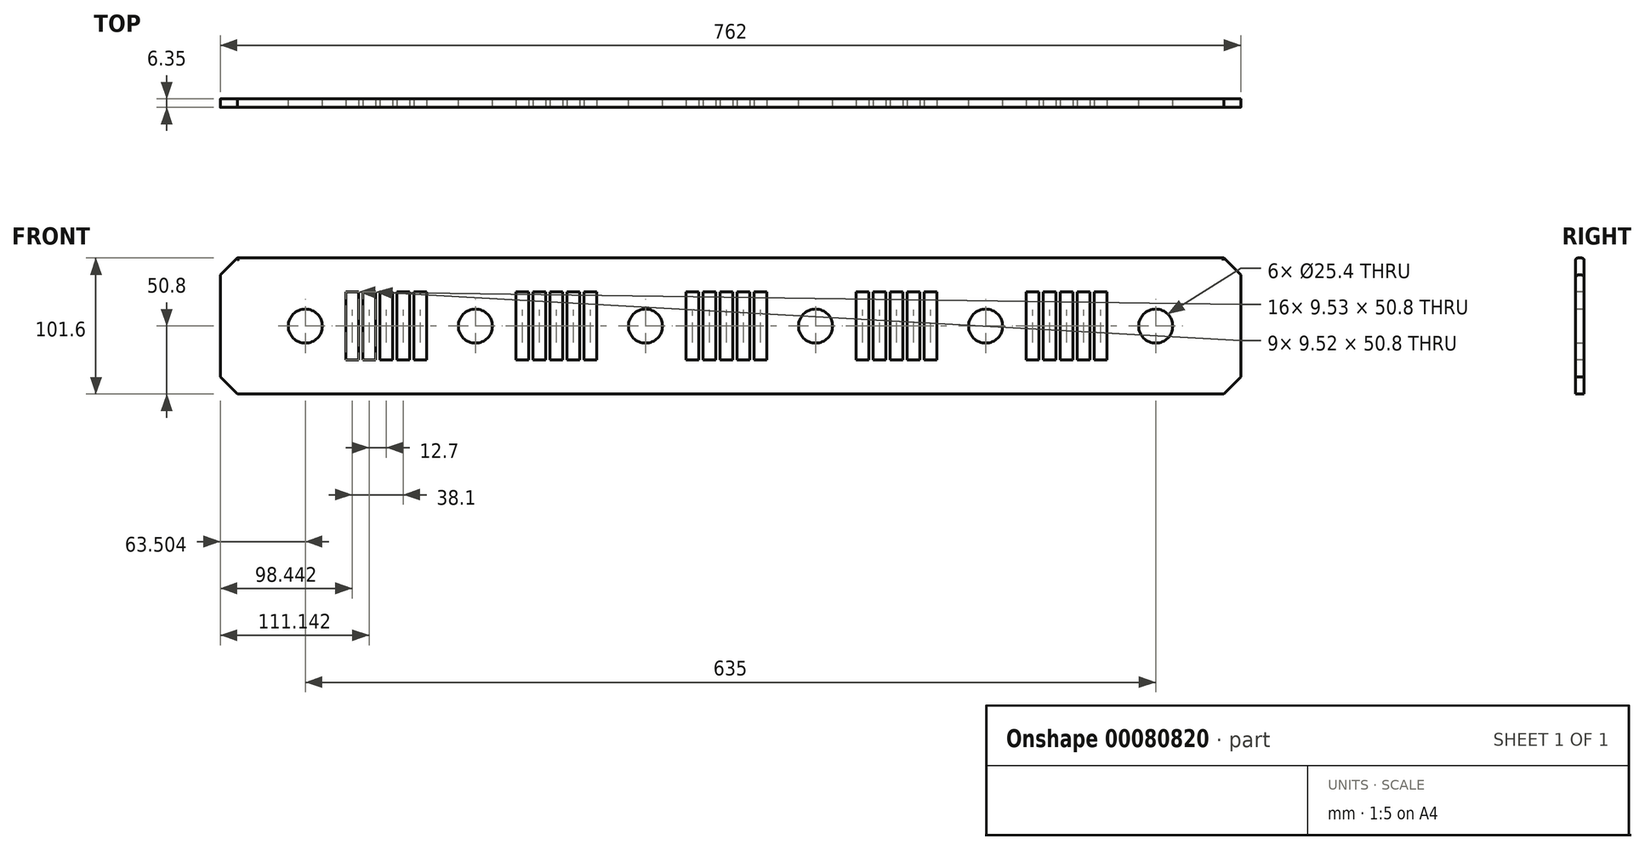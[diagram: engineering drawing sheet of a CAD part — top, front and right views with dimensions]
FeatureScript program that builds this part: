
annotation { "Feature Type Name" : "Feature", "Feature Type Description" : "" }
export const myFeature = defineFeature(function(context is Context, id is Id, definition is map)
    precondition{}
    {
        {
            var Q0;
            Q0=qCreatedBy(makeId("Front.planeOp"),FACE);
            var sketch = newSketch(context, id + "F0", { "sketchPlane" : qUnion([Q0])});
            skLineSegment(sketch, "E0.bottom", {"start": v(-379.3, -37.77) * mm, "end": v(382.7, -37.77) * mm});
            skLineSegment(sketch, "E0.top", {"start": v(-379.3, -139.37) * mm, "end": v(382.7, -139.37) * mm});
            skLineSegment(sketch, "E0.left", {"start": v(-379.3, -37.77) * mm, "end": v(-379.3, -139.37) * mm});
            skLineSegment(sketch, "E0.right", {"start": v(382.7, -37.77) * mm, "end": v(382.7, -139.37) * mm});
            skCircle(sketch, "E1", {"center": v(-315.8, -88.57) * mm, "radius": 12.7 * mm});
            skPoint(sketch, "E1.centerSnap0", {"position": v(-379.3, -88.57) * mm});
            skCircle(sketch, "E2", {"center": v(-188.8, -88.57) * mm, "radius": 12.7 * mm});
            skCircle(sketch, "E3", {"center": v(-61.8, -88.57) * mm, "radius": 12.7 * mm});
            skCircle(sketch, "E4", {"center": v(65.2, -88.57) * mm, "radius": 12.7 * mm});
            skCircle(sketch, "E5", {"center": v(192.2, -88.57) * mm, "radius": 12.7 * mm});
            skCircle(sketch, "E6", {"center": v(319.2, -88.57) * mm, "radius": 12.7 * mm});
            skSolve(sketch);
        }
        {
            var Q0;
            Q0 = qSketchRegion(id + "F0", true);
            extrude(context, id + "F1", {"entities" : qUnion([Q0]), "depth" : 6.35 * mm});
        }
        {
            var Q0;
            Q0=makeQuery(id+"F1.opExtrude","CAP_FACE",FACE,{"disambiguationData":[OSD([sQuery(id+"F0.wireOp",EDGE,"E0.bottom"),sQuery(id+"F0.wireOp",EDGE,"E0.top"),sQuery(id+"F0.wireOp",EDGE,"E0.left"),sQuery(id+"F0.wireOp",EDGE,"E0.right"),sQuery(id+"F0.wireOp",EDGE,"E1"),sQuery(id+"F0.wireOp",EDGE,"E2"),sQuery(id+"F0.wireOp",EDGE,"E3"),sQuery(id+"F0.wireOp",EDGE,"E4"),sQuery(id+"F0.wireOp",EDGE,"E5"),sQuery(id+"F0.wireOp",EDGE,"E6")])],"isStart":false});
            var sketch = newSketch(context, id + "F2", { "sketchPlane" : qUnion([Q0])});
            skLineSegment(sketch, "E7.bottom", {"start": v(-285.62, -63.17) * mm, "end": v(-276.1, -63.17) * mm});
            skLineSegment(sketch, "E7.top", {"start": v(-285.62, -113.97) * mm, "end": v(-276.1, -113.97) * mm});
            skLineSegment(sketch, "E7.left", {"start": v(-285.62, -63.17) * mm, "end": v(-285.62, -113.97) * mm});
            skLineSegment(sketch, "E7.right", {"start": v(-276.1, -63.17) * mm, "end": v(-276.1, -113.97) * mm});
            skLineSegment(sketch, "E8.1.0.0", {"start": v(-263.4, -63.17) * mm, "end": v(-263.4, -113.97) * mm});
            skLineSegment(sketch, "E8.1.0.1", {"start": v(-272.92, -113.97) * mm, "end": v(-263.4, -113.97) * mm});
            skLineSegment(sketch, "E8.1.0.2", {"start": v(-272.92, -63.17) * mm, "end": v(-263.4, -63.17) * mm});
            skLineSegment(sketch, "E8.1.0.3", {"start": v(-272.92, -63.17) * mm, "end": v(-272.92, -113.97) * mm});
            skLineSegment(sketch, "E8.2.0.0", {"start": v(-250.7, -63.17) * mm, "end": v(-250.7, -113.97) * mm});
            skLineSegment(sketch, "E8.2.0.1", {"start": v(-260.22, -113.97) * mm, "end": v(-250.7, -113.97) * mm});
            skLineSegment(sketch, "E8.2.0.2", {"start": v(-260.22, -63.17) * mm, "end": v(-250.7, -63.17) * mm});
            skLineSegment(sketch, "E8.2.0.3", {"start": v(-260.22, -63.17) * mm, "end": v(-260.22, -113.97) * mm});
            skLineSegment(sketch, "E8.3.0.0", {"start": v(-238, -63.17) * mm, "end": v(-238, -113.97) * mm});
            skLineSegment(sketch, "E8.3.0.1", {"start": v(-247.52, -113.97) * mm, "end": v(-238, -113.97) * mm});
            skLineSegment(sketch, "E8.3.0.2", {"start": v(-247.52, -63.17) * mm, "end": v(-238, -63.17) * mm});
            skLineSegment(sketch, "E8.3.0.3", {"start": v(-247.52, -63.17) * mm, "end": v(-247.52, -113.97) * mm});
            skLineSegment(sketch, "E8.4.0.0", {"start": v(-225.3, -63.17) * mm, "end": v(-225.3, -113.97) * mm});
            skLineSegment(sketch, "E8.4.0.1", {"start": v(-234.82, -113.97) * mm, "end": v(-225.3, -113.97) * mm});
            skLineSegment(sketch, "E8.4.0.2", {"start": v(-234.82, -63.17) * mm, "end": v(-225.3, -63.17) * mm});
            skLineSegment(sketch, "E8.4.0.3", {"start": v(-234.82, -63.17) * mm, "end": v(-234.82, -113.97) * mm});
            skLineSegment(sketch, "E8.direction1", {"start": v(-276.1, -113.97) * mm, "end": v(-263.4, -113.97) * mm, "construction": true});
            skLineSegment(sketch, "E9.bottom", {"start": v(-31.62, -63.17) * mm, "end": v(-22.1, -63.17) * mm});
            skLineSegment(sketch, "E9.top", {"start": v(-31.62, -113.97) * mm, "end": v(-22.1, -113.97) * mm});
            skLineSegment(sketch, "E9.left", {"start": v(-31.62, -63.17) * mm, "end": v(-31.62, -113.97) * mm});
            skLineSegment(sketch, "E9.right", {"start": v(-22.1, -63.17) * mm, "end": v(-22.1, -113.97) * mm});
            skLineSegment(sketch, "E10.1.0.0", {"start": v(-9.4, -63.17) * mm, "end": v(-9.4, -113.97) * mm});
            skLineSegment(sketch, "E10.1.0.1", {"start": v(-18.92, -113.97) * mm, "end": v(-9.4, -113.97) * mm});
            skLineSegment(sketch, "E10.1.0.2", {"start": v(-18.92, -63.17) * mm, "end": v(-9.4, -63.17) * mm});
            skLineSegment(sketch, "E10.1.0.3", {"start": v(-18.92, -63.17) * mm, "end": v(-18.92, -113.97) * mm});
            skLineSegment(sketch, "E10.2.0.0", {"start": v(3.3, -63.17) * mm, "end": v(3.3, -113.97) * mm});
            skLineSegment(sketch, "E10.2.0.1", {"start": v(-6.22, -113.97) * mm, "end": v(3.3, -113.97) * mm});
            skLineSegment(sketch, "E10.2.0.2", {"start": v(-6.22, -63.17) * mm, "end": v(3.3, -63.17) * mm});
            skLineSegment(sketch, "E10.2.0.3", {"start": v(-6.22, -63.17) * mm, "end": v(-6.22, -113.97) * mm});
            skLineSegment(sketch, "E10.3.0.0", {"start": v(16, -63.17) * mm, "end": v(16, -113.97) * mm});
            skLineSegment(sketch, "E10.3.0.1", {"start": v(6.48, -113.97) * mm, "end": v(16, -113.97) * mm});
            skLineSegment(sketch, "E10.3.0.2", {"start": v(6.48, -63.17) * mm, "end": v(16, -63.17) * mm});
            skLineSegment(sketch, "E10.3.0.3", {"start": v(6.48, -63.17) * mm, "end": v(6.48, -113.97) * mm});
            skLineSegment(sketch, "E10.4.0.0", {"start": v(28.7, -63.17) * mm, "end": v(28.7, -113.97) * mm});
            skLineSegment(sketch, "E10.4.0.1", {"start": v(19.18, -113.97) * mm, "end": v(28.7, -113.97) * mm});
            skLineSegment(sketch, "E10.4.0.2", {"start": v(19.18, -63.17) * mm, "end": v(28.7, -63.17) * mm});
            skLineSegment(sketch, "E10.4.0.3", {"start": v(19.18, -63.17) * mm, "end": v(19.18, -113.97) * mm});
            skLineSegment(sketch, "E10.direction1", {"start": v(-22.1, -113.97) * mm, "end": v(-9.4, -113.97) * mm, "construction": true});
            skLineSegment(sketch, "E11.bottom", {"start": v(95.38, -63.17) * mm, "end": v(104.9, -63.17) * mm});
            skLineSegment(sketch, "E11.top", {"start": v(95.38, -113.97) * mm, "end": v(104.9, -113.97) * mm});
            skLineSegment(sketch, "E11.left", {"start": v(95.38, -63.17) * mm, "end": v(95.38, -113.97) * mm});
            skLineSegment(sketch, "E11.right", {"start": v(104.9, -63.17) * mm, "end": v(104.9, -113.97) * mm});
            skLineSegment(sketch, "E12.1.0.0", {"start": v(117.6, -63.17) * mm, "end": v(117.6, -113.97) * mm});
            skLineSegment(sketch, "E12.1.0.1", {"start": v(108.08, -113.97) * mm, "end": v(117.6, -113.97) * mm});
            skLineSegment(sketch, "E12.1.0.2", {"start": v(108.08, -63.17) * mm, "end": v(117.6, -63.17) * mm});
            skLineSegment(sketch, "E12.1.0.3", {"start": v(108.08, -63.17) * mm, "end": v(108.08, -113.97) * mm});
            skLineSegment(sketch, "E12.2.0.0", {"start": v(130.3, -63.17) * mm, "end": v(130.3, -113.97) * mm});
            skLineSegment(sketch, "E12.2.0.1", {"start": v(120.78, -113.97) * mm, "end": v(130.3, -113.97) * mm});
            skLineSegment(sketch, "E12.2.0.2", {"start": v(120.78, -63.17) * mm, "end": v(130.3, -63.17) * mm});
            skLineSegment(sketch, "E12.2.0.3", {"start": v(120.78, -63.17) * mm, "end": v(120.78, -113.97) * mm});
            skLineSegment(sketch, "E12.3.0.0", {"start": v(143, -63.17) * mm, "end": v(143, -113.97) * mm});
            skLineSegment(sketch, "E12.3.0.1", {"start": v(133.48, -113.97) * mm, "end": v(143, -113.97) * mm});
            skLineSegment(sketch, "E12.3.0.2", {"start": v(133.48, -63.17) * mm, "end": v(143, -63.17) * mm});
            skLineSegment(sketch, "E12.3.0.3", {"start": v(133.48, -63.17) * mm, "end": v(133.48, -113.97) * mm});
            skLineSegment(sketch, "E12.4.0.0", {"start": v(155.7, -63.17) * mm, "end": v(155.7, -113.97) * mm});
            skLineSegment(sketch, "E12.4.0.1", {"start": v(146.18, -113.97) * mm, "end": v(155.7, -113.97) * mm});
            skLineSegment(sketch, "E12.4.0.2", {"start": v(146.18, -63.17) * mm, "end": v(155.7, -63.17) * mm});
            skLineSegment(sketch, "E12.4.0.3", {"start": v(146.18, -63.17) * mm, "end": v(146.18, -113.97) * mm});
            skLineSegment(sketch, "E12.direction1", {"start": v(104.9, -113.97) * mm, "end": v(117.6, -113.97) * mm, "construction": true});
            skLineSegment(sketch, "E13.bottom", {"start": v(222.38, -63.17) * mm, "end": v(231.9, -63.17) * mm});
            skLineSegment(sketch, "E13.top", {"start": v(222.38, -113.97) * mm, "end": v(231.9, -113.97) * mm});
            skLineSegment(sketch, "E13.left", {"start": v(222.38, -63.17) * mm, "end": v(222.38, -113.97) * mm});
            skLineSegment(sketch, "E13.right", {"start": v(231.9, -63.17) * mm, "end": v(231.9, -113.97) * mm});
            skLineSegment(sketch, "E14.1.0.0", {"start": v(244.6, -63.17) * mm, "end": v(244.6, -113.97) * mm});
            skLineSegment(sketch, "E14.1.0.1", {"start": v(235.08, -113.97) * mm, "end": v(244.6, -113.97) * mm});
            skLineSegment(sketch, "E14.1.0.2", {"start": v(235.08, -63.17) * mm, "end": v(244.6, -63.17) * mm});
            skLineSegment(sketch, "E14.1.0.3", {"start": v(235.08, -63.17) * mm, "end": v(235.08, -113.97) * mm});
            skLineSegment(sketch, "E14.2.0.0", {"start": v(257.3, -63.17) * mm, "end": v(257.3, -113.97) * mm});
            skLineSegment(sketch, "E14.2.0.1", {"start": v(247.78, -113.97) * mm, "end": v(257.3, -113.97) * mm});
            skLineSegment(sketch, "E14.2.0.2", {"start": v(247.78, -63.17) * mm, "end": v(257.3, -63.17) * mm});
            skLineSegment(sketch, "E14.2.0.3", {"start": v(247.78, -63.17) * mm, "end": v(247.78, -113.97) * mm});
            skLineSegment(sketch, "E14.3.0.0", {"start": v(270, -63.17) * mm, "end": v(270, -113.97) * mm});
            skLineSegment(sketch, "E14.3.0.1", {"start": v(260.48, -113.97) * mm, "end": v(270, -113.97) * mm});
            skLineSegment(sketch, "E14.3.0.2", {"start": v(260.48, -63.17) * mm, "end": v(270, -63.17) * mm});
            skLineSegment(sketch, "E14.3.0.3", {"start": v(260.48, -63.17) * mm, "end": v(260.48, -113.97) * mm});
            skLineSegment(sketch, "E14.4.0.0", {"start": v(282.7, -63.17) * mm, "end": v(282.7, -113.97) * mm});
            skLineSegment(sketch, "E14.4.0.1", {"start": v(273.18, -113.97) * mm, "end": v(282.7, -113.97) * mm});
            skLineSegment(sketch, "E14.4.0.2", {"start": v(273.18, -63.17) * mm, "end": v(282.7, -63.17) * mm});
            skLineSegment(sketch, "E14.4.0.3", {"start": v(273.18, -63.17) * mm, "end": v(273.18, -113.97) * mm});
            skLineSegment(sketch, "E14.direction1", {"start": v(231.9, -113.97) * mm, "end": v(244.6, -113.97) * mm, "construction": true});
            skLineSegment(sketch, "E15.bottom", {"start": v(-158.62, -63.17) * mm, "end": v(-149.1, -63.17) * mm});
            skLineSegment(sketch, "E15.top", {"start": v(-158.62, -113.97) * mm, "end": v(-149.1, -113.97) * mm});
            skLineSegment(sketch, "E15.left", {"start": v(-158.62, -63.17) * mm, "end": v(-158.62, -113.97) * mm});
            skLineSegment(sketch, "E15.right", {"start": v(-149.1, -63.17) * mm, "end": v(-149.1, -113.97) * mm});
            skLineSegment(sketch, "E16.1.0.0", {"start": v(-136.4, -63.17) * mm, "end": v(-136.4, -113.97) * mm});
            skLineSegment(sketch, "E16.1.0.1", {"start": v(-145.92, -113.97) * mm, "end": v(-136.4, -113.97) * mm});
            skLineSegment(sketch, "E16.1.0.2", {"start": v(-145.92, -63.17) * mm, "end": v(-136.4, -63.17) * mm});
            skLineSegment(sketch, "E16.1.0.3", {"start": v(-145.92, -63.17) * mm, "end": v(-145.92, -113.97) * mm});
            skLineSegment(sketch, "E16.2.0.0", {"start": v(-123.7, -63.17) * mm, "end": v(-123.7, -113.97) * mm});
            skLineSegment(sketch, "E16.2.0.1", {"start": v(-133.22, -113.97) * mm, "end": v(-123.7, -113.97) * mm});
            skLineSegment(sketch, "E16.2.0.2", {"start": v(-133.22, -63.17) * mm, "end": v(-123.7, -63.17) * mm});
            skLineSegment(sketch, "E16.2.0.3", {"start": v(-133.22, -63.17) * mm, "end": v(-133.22, -113.97) * mm});
            skLineSegment(sketch, "E16.3.0.0", {"start": v(-111, -63.17) * mm, "end": v(-111, -113.97) * mm});
            skLineSegment(sketch, "E16.3.0.1", {"start": v(-120.52, -113.97) * mm, "end": v(-111, -113.97) * mm});
            skLineSegment(sketch, "E16.3.0.2", {"start": v(-120.52, -63.17) * mm, "end": v(-111, -63.17) * mm});
            skLineSegment(sketch, "E16.3.0.3", {"start": v(-120.52, -63.17) * mm, "end": v(-120.52, -113.97) * mm});
            skLineSegment(sketch, "E16.4.0.0", {"start": v(-98.3, -63.17) * mm, "end": v(-98.3, -113.97) * mm});
            skLineSegment(sketch, "E16.4.0.1", {"start": v(-107.82, -113.97) * mm, "end": v(-98.3, -113.97) * mm});
            skLineSegment(sketch, "E16.4.0.2", {"start": v(-107.82, -63.17) * mm, "end": v(-98.3, -63.17) * mm});
            skLineSegment(sketch, "E16.4.0.3", {"start": v(-107.82, -63.17) * mm, "end": v(-107.82, -113.97) * mm});
            skLineSegment(sketch, "E16.direction1", {"start": v(-149.1, -113.97) * mm, "end": v(-136.4, -113.97) * mm, "construction": true});
            skSolve(sketch);
        }
        {
            var Q0;
            Q0 = qSketchRegion(id + "F2", true);
            extrude(context, id + "F3", {"entities" : qUnion([Q0]), "operationType" : NewBodyOperationType.REMOVE, "endBound" : BoundingType.THROUGH_ALL, "oppositeDirection" : true, "depth" : 25.4 * mm});
        }
        {
            var Q0;
            Q0=makeQuery(id+"F1.opExtrude","SWEPT_EDGE",EDGE,{"disambiguationData":[OSD([sQuery(id+"F0.wireOp",EDGE,"E0.bottom"),sQuery(id+"F0.wireOp",EDGE,"E0.left")])]});
            var Q1;
            Q1=makeQuery(id+"F1.opExtrude","SWEPT_EDGE",EDGE,{"disambiguationData":[OSD([sQuery(id+"F0.wireOp",EDGE,"E0.top"),sQuery(id+"F0.wireOp",EDGE,"E0.left")])]});
            var Q2;
            Q2=makeQuery(id+"F1.opExtrude","SWEPT_EDGE",EDGE,{"disambiguationData":[OSD([sQuery(id+"F0.wireOp",EDGE,"E0.bottom"),sQuery(id+"F0.wireOp",EDGE,"E0.right")])]});
            var Q3;
            Q3=makeQuery(id+"F1.opExtrude","SWEPT_EDGE",EDGE,{"disambiguationData":[OSD([sQuery(id+"F0.wireOp",EDGE,"E0.top"),sQuery(id+"F0.wireOp",EDGE,"E0.right")])]});
            chamfer(context, id + "F4", {"entities" : qUnion([Q0, Q1, Q2, Q3]), "width" : 12.7 * mm, "tangentPropagation" : true});
        }
        {
            var Q0;
            Q0=makeQuery(id+"F1.opExtrude","CAP_EDGE",EDGE,{"disambiguationData":[OSD([sQuery(id+"F0.wireOp",EDGE,"E0.bottom")])],"isStart":false});
            var Q1;
            Q1=makeQuery(id+"F1.opExtrude","CAP_EDGE",EDGE,{"disambiguationData":[OSD([sQuery(id+"F0.wireOp",EDGE,"E0.bottom")])],"isStart":true});
            var Q2;
            {var subQ0=sQuery(id+"F0.wireOp",EDGE,"E0.left");var subQ1=sQuery(id+"F0.wireOp",EDGE,"E0.bottom");Q2=makeQuery(id+"F4.opChamfer","BLEND_EDGE",EDGE,{"blendedFrom":[makeQuery(id+"F1.opExtrude","SWEPT_EDGE",EDGE,{"disambiguationData":[OSD([subQ1,subQ0])]}),makeQuery(id+"F1.opExtrude","CAP_FACE",FACE,{"disambiguationData":[OSD([subQ1,sQuery(id+"F0.wireOp",EDGE,"E0.top"),subQ0,sQuery(id+"F0.wireOp",EDGE,"E0.right"),sQuery(id+"F0.wireOp",EDGE,"E1"),sQuery(id+"F0.wireOp",EDGE,"E2"),sQuery(id+"F0.wireOp",EDGE,"E3"),sQuery(id+"F0.wireOp",EDGE,"E4"),sQuery(id+"F0.wireOp",EDGE,"E5"),sQuery(id+"F0.wireOp",EDGE,"E6")])],"isStart":false})],"blendedInto":[makeQuery(id+"F1.opExtrude","CAP_FACE",FACE,{"disambiguationData":[OSD([subQ1,sQuery(id+"F0.wireOp",EDGE,"E0.top"),subQ0,sQuery(id+"F0.wireOp",EDGE,"E0.right"),sQuery(id+"F0.wireOp",EDGE,"E1"),sQuery(id+"F0.wireOp",EDGE,"E2"),sQuery(id+"F0.wireOp",EDGE,"E3"),sQuery(id+"F0.wireOp",EDGE,"E4"),sQuery(id+"F0.wireOp",EDGE,"E5"),sQuery(id+"F0.wireOp",EDGE,"E6")])],"isStart":false})]});}
            var Q3;
            {var subQ0=sQuery(id+"F0.wireOp",EDGE,"E0.left");var subQ1=sQuery(id+"F0.wireOp",EDGE,"E0.bottom");Q3=makeQuery(id+"F4.opChamfer","BLEND_EDGE",EDGE,{"blendedFrom":[makeQuery(id+"F1.opExtrude","SWEPT_EDGE",EDGE,{"disambiguationData":[OSD([subQ1,subQ0])]}),makeQuery(id+"F1.opExtrude","CAP_FACE",FACE,{"disambiguationData":[OSD([subQ1,sQuery(id+"F0.wireOp",EDGE,"E0.top"),subQ0,sQuery(id+"F0.wireOp",EDGE,"E0.right"),sQuery(id+"F0.wireOp",EDGE,"E1"),sQuery(id+"F0.wireOp",EDGE,"E2"),sQuery(id+"F0.wireOp",EDGE,"E3"),sQuery(id+"F0.wireOp",EDGE,"E4"),sQuery(id+"F0.wireOp",EDGE,"E5"),sQuery(id+"F0.wireOp",EDGE,"E6")])],"isStart":true})],"blendedInto":[makeQuery(id+"F1.opExtrude","CAP_FACE",FACE,{"disambiguationData":[OSD([subQ1,sQuery(id+"F0.wireOp",EDGE,"E0.top"),subQ0,sQuery(id+"F0.wireOp",EDGE,"E0.right"),sQuery(id+"F0.wireOp",EDGE,"E1"),sQuery(id+"F0.wireOp",EDGE,"E2"),sQuery(id+"F0.wireOp",EDGE,"E3"),sQuery(id+"F0.wireOp",EDGE,"E4"),sQuery(id+"F0.wireOp",EDGE,"E5"),sQuery(id+"F0.wireOp",EDGE,"E6")])],"isStart":true})]});}
            var Q4;
            {var subQ0=sQuery(id+"F0.wireOp",EDGE,"E0.right");var subQ1=sQuery(id+"F0.wireOp",EDGE,"E0.bottom");Q4=makeQuery(id+"F4.opChamfer","BLEND_EDGE",EDGE,{"blendedFrom":[makeQuery(id+"F1.opExtrude","SWEPT_EDGE",EDGE,{"disambiguationData":[OSD([subQ1,subQ0])]}),makeQuery(id+"F1.opExtrude","CAP_FACE",FACE,{"disambiguationData":[OSD([subQ1,sQuery(id+"F0.wireOp",EDGE,"E0.top"),sQuery(id+"F0.wireOp",EDGE,"E0.left"),subQ0,sQuery(id+"F0.wireOp",EDGE,"E1"),sQuery(id+"F0.wireOp",EDGE,"E2"),sQuery(id+"F0.wireOp",EDGE,"E3"),sQuery(id+"F0.wireOp",EDGE,"E4"),sQuery(id+"F0.wireOp",EDGE,"E5"),sQuery(id+"F0.wireOp",EDGE,"E6")])],"isStart":true})],"blendedInto":[makeQuery(id+"F1.opExtrude","CAP_FACE",FACE,{"disambiguationData":[OSD([subQ1,sQuery(id+"F0.wireOp",EDGE,"E0.top"),sQuery(id+"F0.wireOp",EDGE,"E0.left"),subQ0,sQuery(id+"F0.wireOp",EDGE,"E1"),sQuery(id+"F0.wireOp",EDGE,"E2"),sQuery(id+"F0.wireOp",EDGE,"E3"),sQuery(id+"F0.wireOp",EDGE,"E4"),sQuery(id+"F0.wireOp",EDGE,"E5"),sQuery(id+"F0.wireOp",EDGE,"E6")])],"isStart":true})]});}
            var Q5;
            {var subQ0=sQuery(id+"F0.wireOp",EDGE,"E0.right");var subQ1=sQuery(id+"F0.wireOp",EDGE,"E0.bottom");Q5=makeQuery(id+"F4.opChamfer","BLEND_EDGE",EDGE,{"blendedFrom":[makeQuery(id+"F1.opExtrude","SWEPT_EDGE",EDGE,{"disambiguationData":[OSD([subQ1,subQ0])]}),makeQuery(id+"F1.opExtrude","CAP_FACE",FACE,{"disambiguationData":[OSD([subQ1,sQuery(id+"F0.wireOp",EDGE,"E0.top"),sQuery(id+"F0.wireOp",EDGE,"E0.left"),subQ0,sQuery(id+"F0.wireOp",EDGE,"E1"),sQuery(id+"F0.wireOp",EDGE,"E2"),sQuery(id+"F0.wireOp",EDGE,"E3"),sQuery(id+"F0.wireOp",EDGE,"E4"),sQuery(id+"F0.wireOp",EDGE,"E5"),sQuery(id+"F0.wireOp",EDGE,"E6")])],"isStart":false})],"blendedInto":[makeQuery(id+"F1.opExtrude","CAP_FACE",FACE,{"disambiguationData":[OSD([subQ1,sQuery(id+"F0.wireOp",EDGE,"E0.top"),sQuery(id+"F0.wireOp",EDGE,"E0.left"),subQ0,sQuery(id+"F0.wireOp",EDGE,"E1"),sQuery(id+"F0.wireOp",EDGE,"E2"),sQuery(id+"F0.wireOp",EDGE,"E3"),sQuery(id+"F0.wireOp",EDGE,"E4"),sQuery(id+"F0.wireOp",EDGE,"E5"),sQuery(id+"F0.wireOp",EDGE,"E6")])],"isStart":false})]});}
            fillet(context, id + "F5", {"entities" : qUnion([Q0, Q1, Q2, Q3, Q4, Q5]), "radius" : 1.6 * mm, "tangentPropagation" : true, "allowEdgeOverflow" : false});
        }
    });
